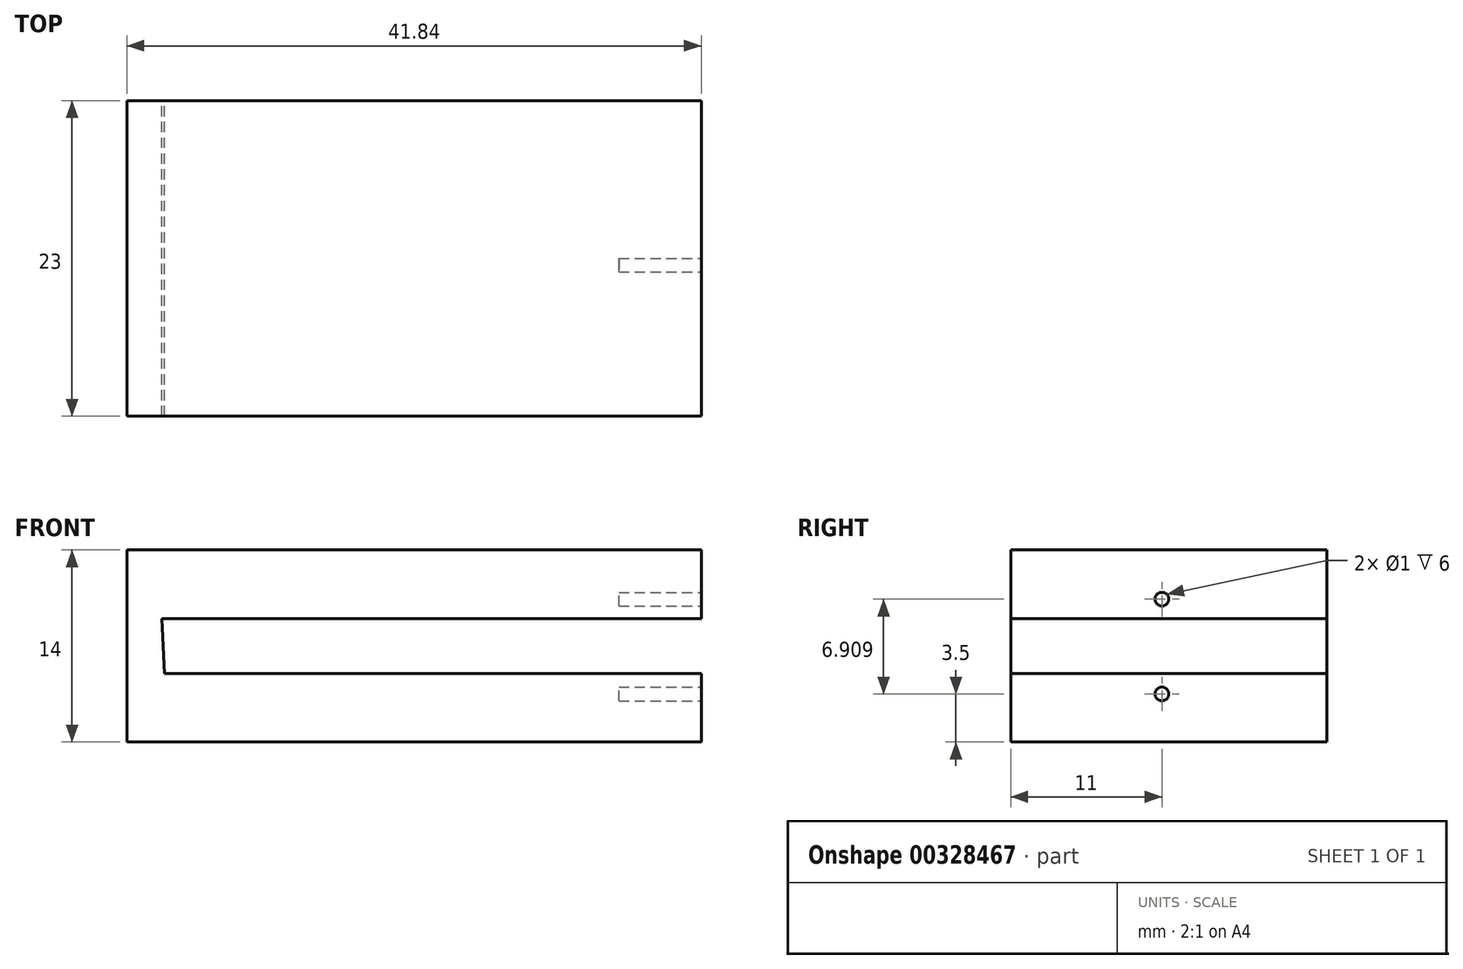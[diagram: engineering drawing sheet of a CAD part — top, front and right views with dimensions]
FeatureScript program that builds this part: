
annotation { "Feature Type Name" : "Feature", "Feature Type Description" : "" }
export const myFeature = defineFeature(function(context is Context, id is Id, definition is map)
    precondition{}
    {
        {
            var Q0;
            Q0=qCreatedBy(makeId("Front.planeOp"),FACE);
            var sketch = newSketch(context, id + "F0", { "sketchPlane" : qUnion([Q0])});
            skLineSegment(sketch, "E0", {"start": v(-41.84, 14) * mm, "end": v(-41.84, 0) * mm});
            skLineSegment(sketch, "E1", {"start": v(-41.84, 0) * mm, "end": v(0, 0) * mm});
            skLineSegment(sketch, "E2", {"start": v(0, 0) * mm, "end": v(0, 5) * mm});
            skLineSegment(sketch, "E3", {"start": v(0, 5) * mm, "end": v(-39.1, 5) * mm});
            skLineSegment(sketch, "E4", {"start": v(-39.1, 5) * mm, "end": v(-39.3, 9) * mm});
            skLineSegment(sketch, "E5", {"start": v(-39.3, 9) * mm, "end": v(0, 9) * mm});
            skLineSegment(sketch, "E6", {"start": v(0, 9) * mm, "end": v(0, 14) * mm});
            skLineSegment(sketch, "E7", {"start": v(0, 14) * mm, "end": v(-41.84, 14) * mm});
            skSolve(sketch);
        }
        {
            var Q0;
            Q0 = qSketchRegion(id + "F0", true);
            extrude(context, id + "F1", {"entities" : qUnion([Q0]), "depth" : 23 * mm});
        }
        {
            var Q0;
            Q0=qCreatedBy(makeId("Right.planeOp"),FACE);
            var sketch = newSketch(context, id + "F2", { "sketchPlane" : qUnion([Q0])});
            skCircle(sketch, "E8", {"center": v(-12, 10.4) * mm, "radius": 0.5 * mm});
            skCircle(sketch, "E9", {"center": v(-12, 3.5) * mm, "radius": 0.5 * mm});
            skSolve(sketch);
        }
        {
            var Q0;
            Q0 = qSketchRegion(id + "F2", true);
            extrude(context, id + "F3", {"entities" : qUnion([Q0]), "operationType" : NewBodyOperationType.REMOVE, "oppositeDirection" : true, "depth" : 6 * mm});
        }
    });
